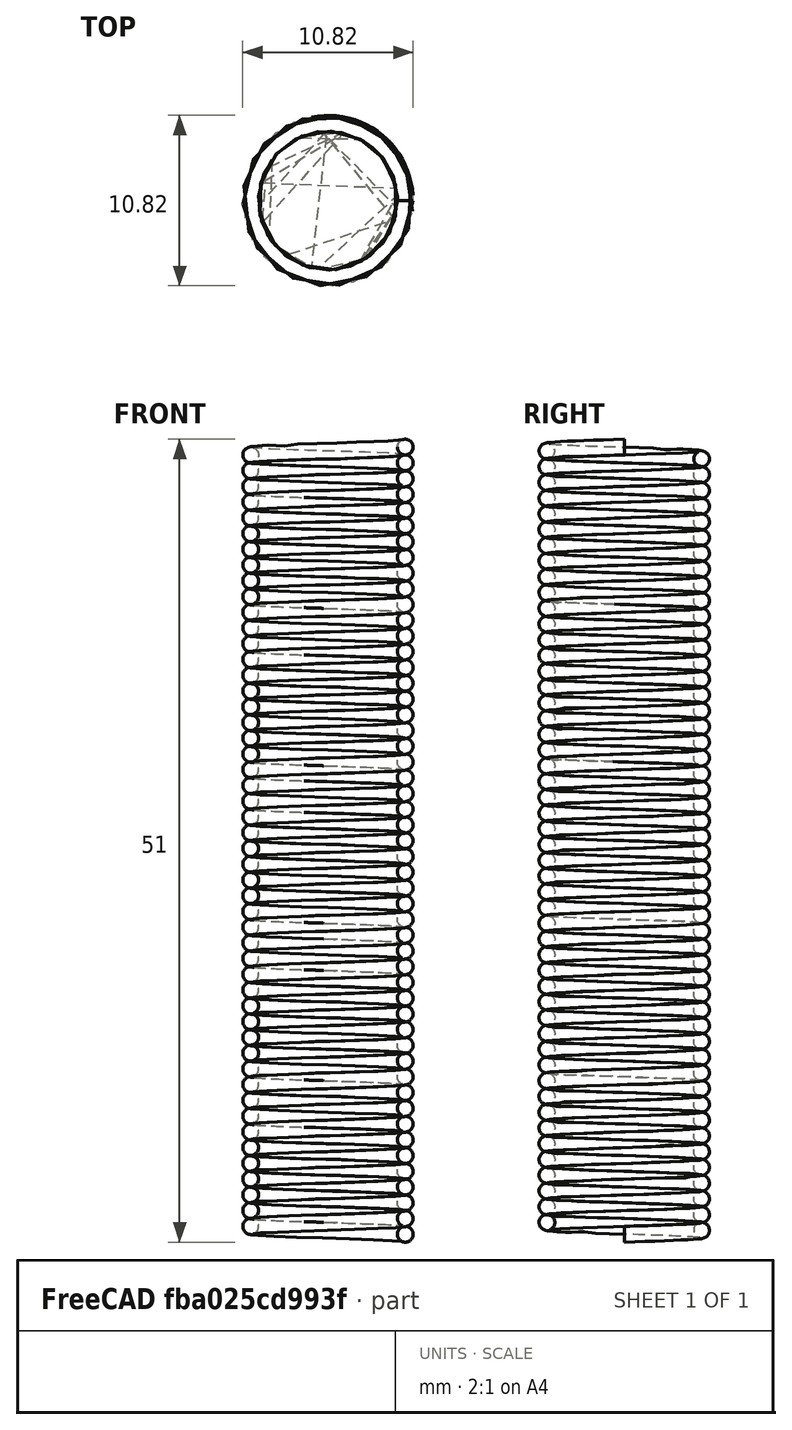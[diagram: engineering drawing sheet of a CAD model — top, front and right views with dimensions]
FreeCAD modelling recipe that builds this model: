
FCSTD DOCUMENT  (FreeCAD 0.21R33771 (Git))
Label: Machine Elment Design_TensionSpring
License: All rights reserved
LicenseURL: http://en.wikipedia.org/wiki/All_rights_reserved
objects: Part::Helix×1, Sketcher::SketchObject×1, PartDesign::Body×1, Part::Sweep×1
note: 4 computed .brp shape members not serialized (recipe doc carries the construction recipe); baked Part::Feature solids carry a one-line shape summary decoded from their .brp

FEATURE [Part::Helix] Helix
  Angle = 0
  AttacherType = Attacher::AttachEngine3D
  Height = 50
  LocalCoord = 0
  Pitch = 1
  Radius = 5
  SegmentLength = 0
  Style = 1
FEATURE [Sketcher::SketchObject] Sketch
  FullyConstrained = false
  MapMode = 5
  Placement = pos=(0,0,0) rot=(1,0,0;1.5708rad)
  Support = -> [XZ_Plane]
  sketch-geometry (1):
    g0: Circle CenterX=4.90889 CenterY=0 CenterZ=0 NormalX=0 NormalY=0 NormalZ=1 AngleXU=0 Radius=0.5
  constraints (2):
    c: PointOnObject(g0,g-1)
    c: Diameter(g0) = 1
FEATURE [PartDesign::Body] Body
  Group = -> [Sketch]
  Origin = -> Origin
FEATURE [Part::Sweep] Sweep
  Frenet = true
  Sections = -> [Sketch]
  Solid = true
  Spine = -> Helix [Edge1]
  Transition = 1
